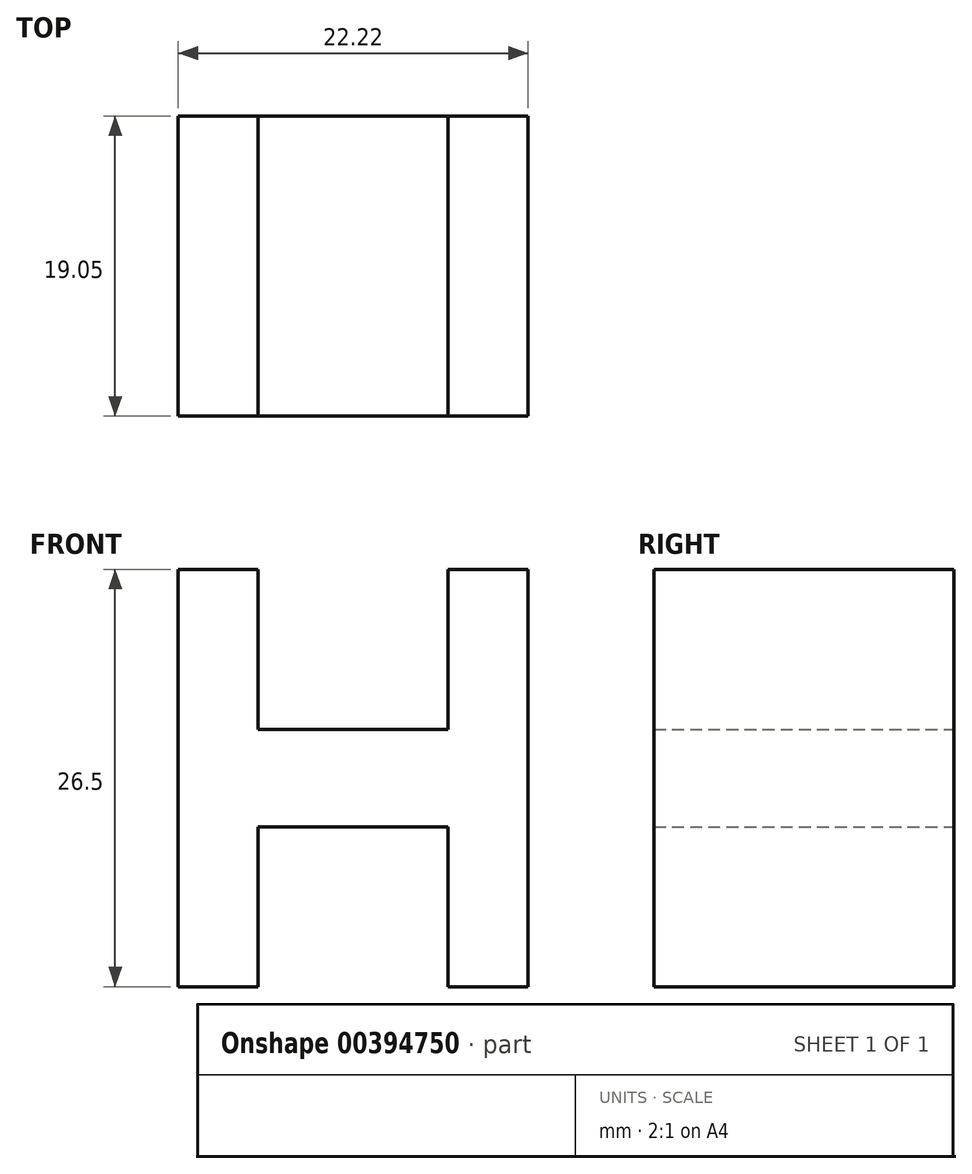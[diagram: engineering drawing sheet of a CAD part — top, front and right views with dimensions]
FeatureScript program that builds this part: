
annotation { "Feature Type Name" : "Feature", "Feature Type Description" : "" }
export const myFeature = defineFeature(function(context is Context, id is Id, definition is map)
    precondition{}
    {
        {
            var Q0;
            Q0=qCreatedBy(makeId("Front.planeOp"),FACE);
            var sketch = newSketch(context, id + "F0", { "sketchPlane" : qUnion([Q0])});
            skLineSegment(sketch, "E0.bottom", {"start": v(-11.11, 3.09) * mm, "end": v(11.11, 3.09) * mm});
            skLineSegment(sketch, "E0.top", {"start": v(-11.11, -3.09) * mm, "end": v(11.11, -3.09) * mm});
            skLineSegment(sketch, "E0.left", {"start": v(-11.11, 3.09) * mm, "end": v(-11.11, -3.09) * mm});
            skLineSegment(sketch, "E0.right", {"start": v(11.11, 3.09) * mm, "end": v(11.11, -3.09) * mm});
            skPoint(sketch, "E0.middle", {"position": v(0, 0) * mm});
            skLineSegment(sketch, "E1.bottom", {"start": v(-11.11, 3.09) * mm, "end": v(-6.03, 3.09) * mm});
            skLineSegment(sketch, "E1.top", {"start": v(-11.11, 13.25) * mm, "end": v(-6.03, 13.25) * mm});
            skLineSegment(sketch, "E1.left", {"start": v(-11.11, 3.09) * mm, "end": v(-11.11, 13.25) * mm});
            skLineSegment(sketch, "E1.right", {"start": v(-6.03, 3.09) * mm, "end": v(-6.03, 13.25) * mm});
            skLineSegment(sketch, "E2.bottom", {"start": v(-11.11, -3.09) * mm, "end": v(-6.03, -3.09) * mm});
            skLineSegment(sketch, "E2.top", {"start": v(-11.11, -13.25) * mm, "end": v(-6.03, -13.25) * mm});
            skLineSegment(sketch, "E2.left", {"start": v(-11.11, -3.09) * mm, "end": v(-11.11, -13.25) * mm});
            skLineSegment(sketch, "E2.right", {"start": v(-6.03, -3.09) * mm, "end": v(-6.03, -13.25) * mm});
            skLineSegment(sketch, "E3.bottom", {"start": v(11.11, 3.09) * mm, "end": v(6.03, 3.09) * mm});
            skLineSegment(sketch, "E3.top", {"start": v(11.11, 13.25) * mm, "end": v(6.03, 13.25) * mm});
            skLineSegment(sketch, "E3.left", {"start": v(11.11, 3.09) * mm, "end": v(11.11, 13.25) * mm});
            skLineSegment(sketch, "E3.right", {"start": v(6.03, 3.09) * mm, "end": v(6.03, 13.25) * mm});
            skLineSegment(sketch, "E4.bottom", {"start": v(11.11, -3.09) * mm, "end": v(6.03, -3.09) * mm});
            skLineSegment(sketch, "E4.top", {"start": v(11.11, -13.25) * mm, "end": v(6.03, -13.25) * mm});
            skLineSegment(sketch, "E4.left", {"start": v(11.11, -3.09) * mm, "end": v(11.11, -13.25) * mm});
            skLineSegment(sketch, "E4.right", {"start": v(6.03, -3.09) * mm, "end": v(6.03, -13.25) * mm});
            skSolve(sketch);
        }
        {
            var Q0;
            Q0=makeQuery(id+"F0.imprint","IMPRINT",FACE,{"disambiguationData":[TD([[makeQuery(id+"F0.imprint","IMPRINT",EDGE,{"derivedFrom":sQuery(id+"F0.wireOp",EDGE,"E2.top")}),1.0]])]});
            var Q1;
            Q1=makeQuery(id+"F0.imprint","IMPRINT",FACE,{"disambiguationData":[TD([[makeQuery(id+"F0.imprint","IMPRINT",EDGE,{"derivedFrom":sQuery(id+"F0.wireOp",EDGE,"E4.top")}),-1.0]])]});
            var Q2;
            Q2=makeQuery(id+"F0.imprint","IMPRINT",FACE,{"disambiguationData":[TD([[makeQuery(id+"F0.imprint","IMPRINT",EDGE,{"derivedFrom":sQuery(id+"F0.wireOp",EDGE,"E1.top")}),-1.0]])]});
            var Q3;
            {var subQ7=sQuery(id+"F0.wireOp",EDGE,"E0.left");Q3=makeQuery(id+"F0.imprint","IMPRINT",FACE,{"disambiguationData":[TD([[makeQuery(id+"F0.imprint","IMPRINT",EDGE,{"derivedFrom":subQ7}),1.0]])]});}
            var Q4;
            Q4=makeQuery(id+"F0.imprint","IMPRINT",FACE,{"disambiguationData":[TD([[makeQuery(id+"F0.imprint","IMPRINT",EDGE,{"derivedFrom":sQuery(id+"F0.wireOp",EDGE,"E3.top")}),1.0]])]});
            extrude(context, id + "F1", {"entities" : qUnion([Q0, Q1, Q2, Q3, Q4]), "depth" : 19.05 * mm, "offsetDistance" : 25.4 * mm});
        }
    });
